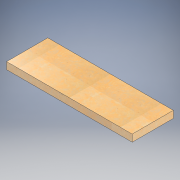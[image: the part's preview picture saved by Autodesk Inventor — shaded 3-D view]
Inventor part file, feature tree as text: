
AUTODESK INVENTOR PART (.ipt)
format: ipt  version: 2022.2 (Build 262287010, 287A)  size: 128,512 bytes
history: native  units: in
note: dims shown in document units (in); Inventor stores cm internally (conversion verified against a paired STEP export)
features: extrude x1, sketch x1
ambient origin geometry x8: Origin, YZ Plane, XZ Plane, XY Plane, X Axis, Y Axis, Z Axis, Center Point
bodies: Solid1 (feature_tree)
feature tree (2):
  extrude  "Extrusion1"  Depth=23.5in
  sketch  "Sketch1"  dims[d0=71.625in d1=23.5in d2=4.0in d3=0.0in]
